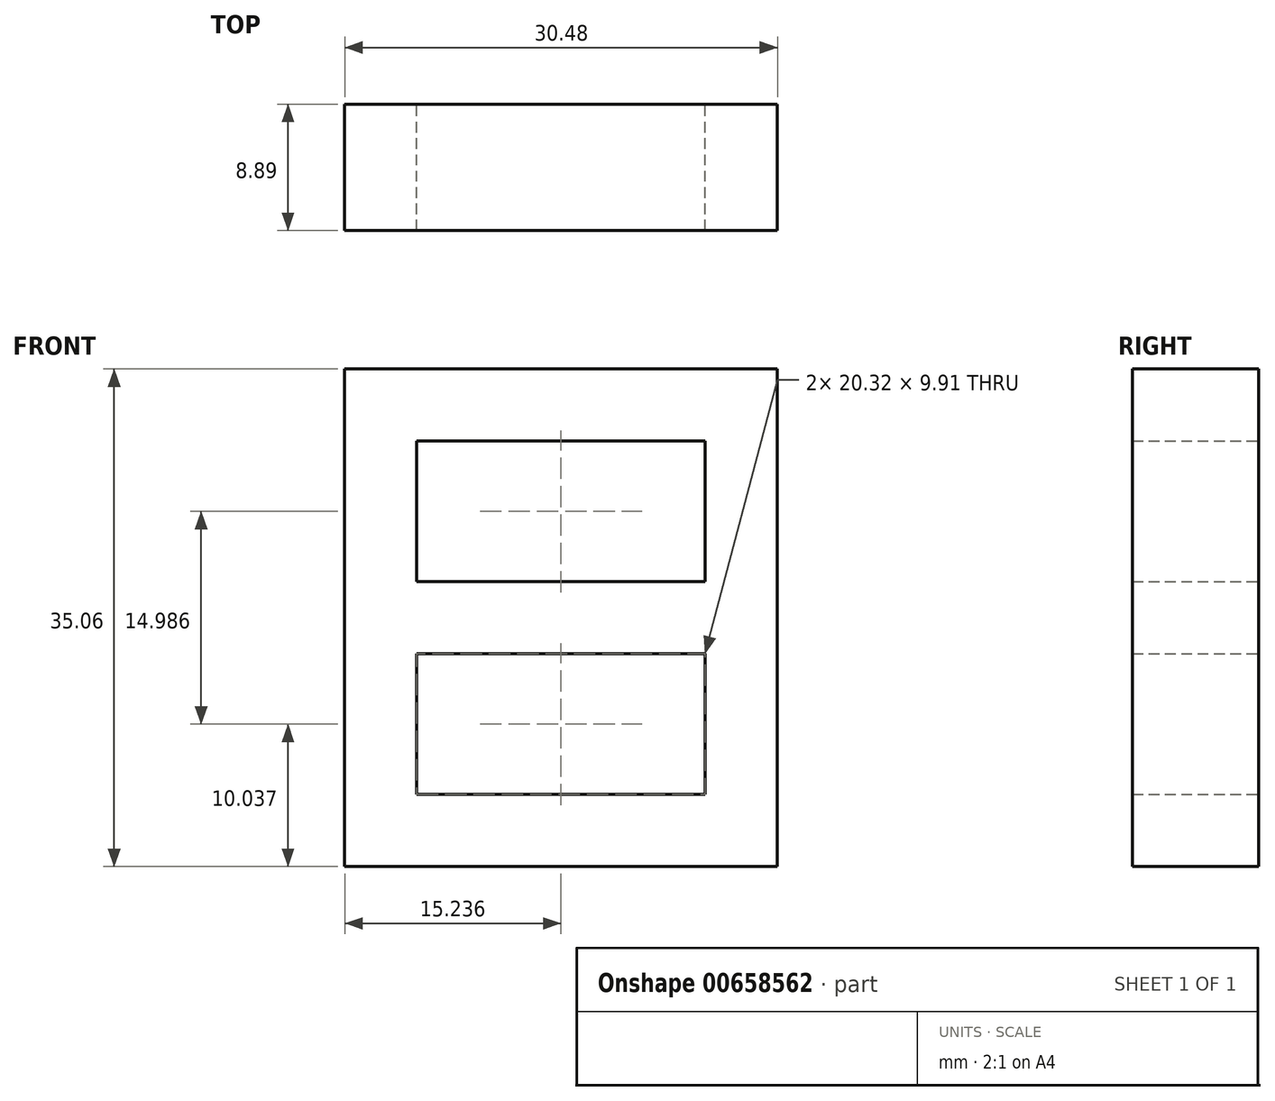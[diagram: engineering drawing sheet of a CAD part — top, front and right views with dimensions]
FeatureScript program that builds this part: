
annotation { "Feature Type Name" : "Feature", "Feature Type Description" : "" }
export const myFeature = defineFeature(function(context is Context, id is Id, definition is map)
    precondition{}
    {
        {
            var Q0;
            Q0=qCreatedBy(makeId("Front.planeOp"),FACE);
            var sketch = newSketch(context, id + "F0", { "sketchPlane" : qUnion([Q0])});
            skLineSegment(sketch, "E0.bottom", {"start": v(-12.9, 19.23) * mm, "end": v(17.58, 19.23) * mm});
            skLineSegment(sketch, "E0.top", {"start": v(-12.9, -15.83) * mm, "end": v(17.58, -15.83) * mm});
            skLineSegment(sketch, "E0.left", {"start": v(-12.9, 19.23) * mm, "end": v(-12.9, -15.83) * mm});
            skLineSegment(sketch, "E0.right", {"start": v(17.58, 19.23) * mm, "end": v(17.58, -15.83) * mm});
            skLineSegment(sketch, "E1.bottom", {"start": v(-7.82, 14.15) * mm, "end": v(12.5, 14.15) * mm});
            skLineSegment(sketch, "E1.top", {"start": v(-7.82, 4.24) * mm, "end": v(12.5, 4.24) * mm});
            skLineSegment(sketch, "E1.left", {"start": v(-7.82, 14.15) * mm, "end": v(-7.82, 4.24) * mm});
            skLineSegment(sketch, "E1.right", {"start": v(12.5, 14.15) * mm, "end": v(12.5, 4.24) * mm});
            skLineSegment(sketch, "E2.bottom", {"start": v(-7.82, -0.84) * mm, "end": v(12.5, -0.84) * mm});
            skLineSegment(sketch, "E2.top", {"start": v(-7.82, -10.75) * mm, "end": v(12.5, -10.75) * mm});
            skLineSegment(sketch, "E2.left", {"start": v(-7.82, -0.84) * mm, "end": v(-7.82, -10.75) * mm});
            skLineSegment(sketch, "E2.right", {"start": v(12.5, -0.84) * mm, "end": v(12.5, -10.75) * mm});
            skSolve(sketch);
        }
        {
            var Q0;
            Q0=makeQuery(id+"F0.imprint","IMPRINT",FACE,{"disambiguationData":[TD([[makeQuery(id+"F0.imprint","IMPRINT",EDGE,{"derivedFrom":sQuery(id+"F0.wireOp",EDGE,"E0.bottom")}),-1.0]])]});
            extrude(context, id + "F1", {"entities" : qUnion([Q0]), "depth" : 8.9 * mm, "offsetDistance" : 25.4 * mm});
        }
    });
